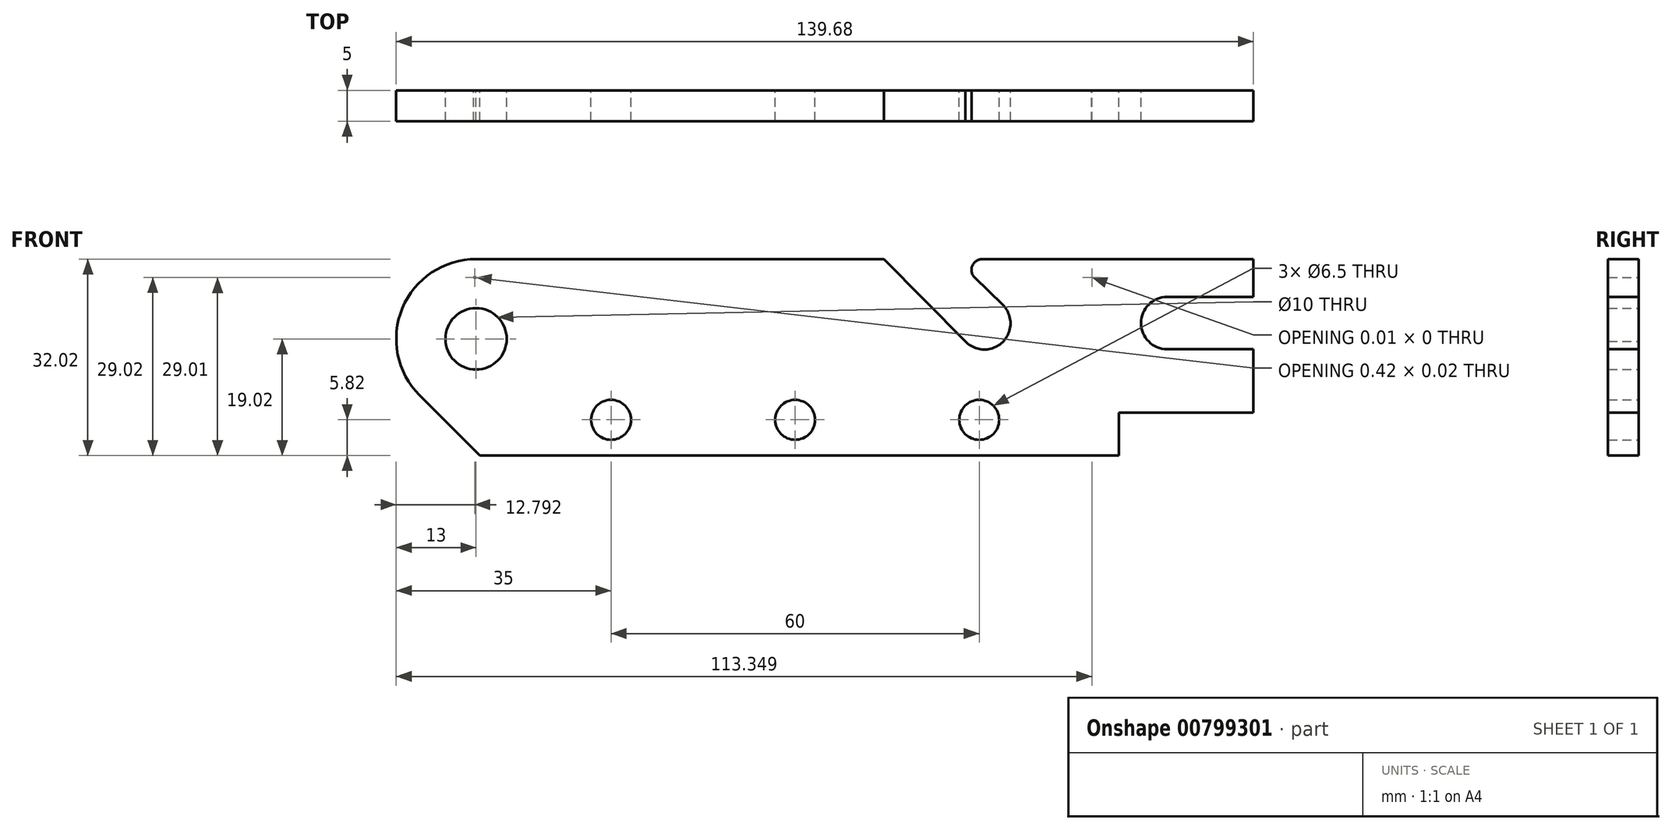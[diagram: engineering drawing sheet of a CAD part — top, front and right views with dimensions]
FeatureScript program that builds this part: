
annotation { "Feature Type Name" : "Feature", "Feature Type Description" : "" }
export const myFeature = defineFeature(function(context is Context, id is Id, definition is map)
    precondition{}
    {
        {
            var Q0;
            Q0=qCreatedBy(makeId("Front.planeOp"),FACE);
            var sketch = newSketch(context, id + "F0", { "sketchPlane" : qUnion([Q0])});
            skPoint(sketch, "E0.middle", {"position": v(0, 0) * mm});
            skCircle(sketch, "E1", {"center": v(-46, 4.1) * mm, "radius": 5 * mm});
            skArc(sketch, "E2", {"start": v(-46, 14.1) * mm, "mid": v(-46.2, 14.1) * mm, "end": v(-46.42, 14.1) * mm});
            skPoint(sketch, "E3", {"position": v(-34, -14.1) * mm});
            skArc(sketch, "E4", {"start": v(63, 7.13) * mm, "mid": v(63, 7.11) * mm, "end": v(63, 7.1) * mm});
            skLineSegment(sketch, "E5.left", {"start": v(-46, 14.1) * mm, "end": v(-46, 14.1) * mm});
            skLineSegment(sketch, "E6", {"start": v(-46, 14.1) * mm, "end": v(-46.42, 14.1) * mm});
            skLineSegment(sketch, "E7", {"start": v(54.35, 14.1) * mm, "end": v(54.35, 14.09) * mm});
            skArc(sketch, "E8", {"start": v(52.29, 12.03) * mm, "mid": v(52.29, 12.02) * mm, "end": v(52.28, 12.02) * mm});
            skLineSegment(sketch, "E9.trimOffspring", {"start": v(54.35, 14.1) * mm, "end": v(54.35, 14.1) * mm});
            skLineSegment(sketch, "E10.trimOffspring", {"start": v(52.29, 12.03) * mm, "end": v(52.28, 12.02) * mm});
            skArc(sketch, "E11.trimOffspring", {"start": v(54.35, 14.09) * mm, "mid": v(54.35, 14.09) * mm, "end": v(54.35, 14.1) * mm});
            skLineSegment(sketch, "E12.top", {"start": v(64.2, -14.1) * mm, "end": v(64.2, -14.1) * mm});
            skPoint(sketch, "E13", {"position": v(55, 4.1) * mm});
            skPoint(sketch, "E14", {"position": v(58.75, -7.9) * mm});
            skLineSegment(sketch, "E15.bottom", {"start": v(58.75, -7.9) * mm, "end": v(68.68, -7.9) * mm});
            skCircle(sketch, "E16", {"center": v(-24, -9.1) * mm, "radius": 3.25 * mm});
            skCircle(sketch, "E17", {"center": v(6, -9.1) * mm, "radius": 3.25 * mm});
            skCircle(sketch, "E18", {"center": v(36, -9.1) * mm, "radius": 3.25 * mm});
            skPoint(sketch, "E19", {"position": v(11.1, 14.1) * mm});
            skPoint(sketch, "E20", {"position": v(68.68, 8.35) * mm});
            skPoint(sketch, "E21", {"position": v(68.68, -0.15) * mm});
            skLineSegment(sketch, "E22", {"start": v(58.75, -7.9) * mm, "end": v(58.75, -14.1) * mm});
            skArc(sketch, "E23", {"start": v(-46, 17.1) * mm, "mid": v(-58.8, 6.36) * mm, "end": v(-50.44, -8.12) * mm});
            skLineSegment(sketch, "E24.top", {"start": v(68.68, -7.9) * mm, "end": v(80.68, -7.9) * mm});
            skLineSegment(sketch, "E24.right", {"start": v(80.68, 14.1) * mm, "end": v(80.68, 10.92) * mm});
            skLineSegment(sketch, "E25", {"start": v(-46, 17.1) * mm, "end": v(20.46, 17.09) * mm});
            skLineSegment(sketch, "E26", {"start": v(80.68, 14.1) * mm, "end": v(80.68, 17.08) * mm});
            skArc(sketch, "E27", {"start": v(33.73, 3.7) * mm, "mid": v(39.81, 3.57) * mm, "end": v(39.8, 9.65) * mm});
            skArc(sketch, "E28", {"start": v(66.63, 10.92) * mm, "mid": v(62.38, 6.67) * mm, "end": v(66.63, 2.42) * mm});
            skLineSegment(sketch, "E29", {"start": v(39.8, 9.65) * mm, "end": v(35.26, 14.1) * mm});
            skLineSegment(sketch, "E30", {"start": v(33.91, 3.53) * mm, "end": v(20.46, 17.09) * mm});
            skLineSegment(sketch, "E31", {"start": v(66.63, 10.92) * mm, "end": v(80.68, 10.92) * mm});
            skLineSegment(sketch, "E32", {"start": v(66.63, 2.42) * mm, "end": v(80.68, 2.42) * mm});
            skLineSegment(sketch, "E33.trimOffspring", {"start": v(36.48, 17.09) * mm, "end": v(80.68, 17.08) * mm});
            skLineSegment(sketch, "E34.trimOffspring", {"start": v(80.68, 2.42) * mm, "end": v(80.68, -7.9) * mm});
            skArc(sketch, "E35", {"start": v(36.48, 17.09) * mm, "mid": v(34.86, 16) * mm, "end": v(35.26, 14.1) * mm});
            skPoint(sketch, "E36.trimOffspring.end.orphan", {"position": v(37.2, 17.09) * mm});
            skPoint(sketch, "E37.start.orphan", {"position": v(35.77, 13.6) * mm});
            skLineSegment(sketch, "E38", {"start": v(-39.9, -14.92) * mm, "end": v(58.75, -14.92) * mm});
            skLineSegment(sketch, "E39", {"start": v(-55.2, -5.1) * mm, "end": v(-45.36, -14.92) * mm});
            skLineSegment(sketch, "E40", {"start": v(-39.9, -14.92) * mm, "end": v(-45.36, -14.92) * mm});
            skLineSegment(sketch, "E41", {"start": v(58.75, -14.1) * mm, "end": v(58.75, -14.92) * mm});
            skPoint(sketch, "E42.orphan", {"position": v(62.6, -14.92) * mm});
            skSolve(sketch);
        }
        {
            var Q0;
            Q0=makeQuery(id+"F0.imprint","IMPRINT",FACE,{"disambiguationData":[TD([[makeQuery(id+"F0.imprint","IMPRINT",EDGE,{"derivedFrom":sQuery(id+"F0.wireOp",EDGE,"E1")}),-1.0]])]});
            extrude(context, id + "F1", {"entities" : qUnion([Q0]), "depth" : 5 * mm, "offsetDistance" : 25 * mm});
        }
    });
